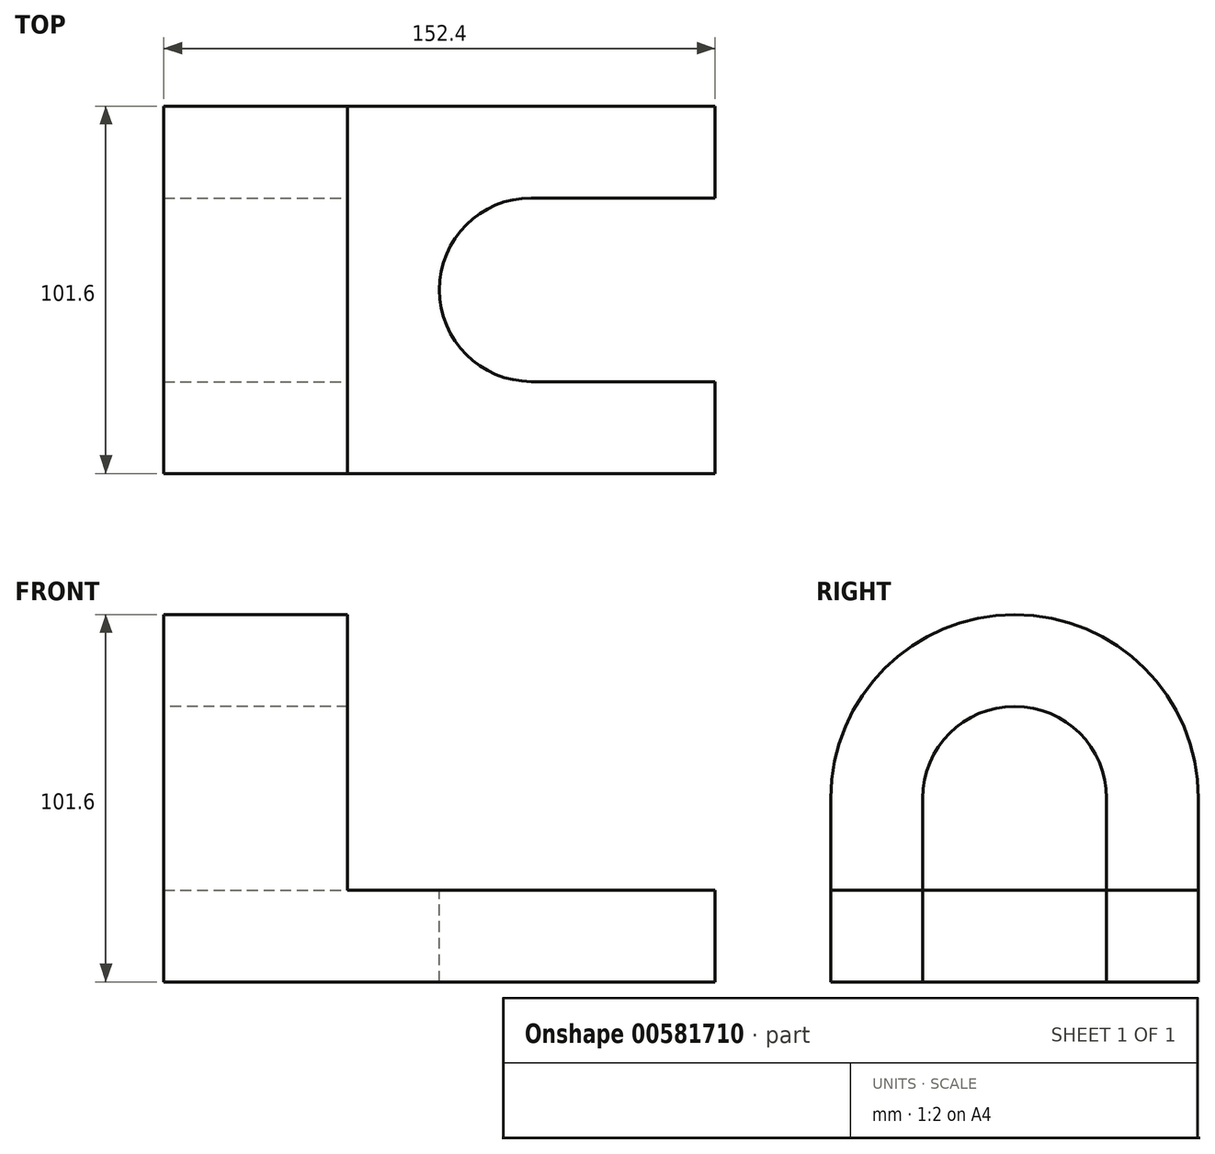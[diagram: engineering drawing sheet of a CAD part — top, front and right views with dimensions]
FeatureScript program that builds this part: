
annotation { "Feature Type Name" : "Feature", "Feature Type Description" : "" }
export const myFeature = defineFeature(function(context is Context, id is Id, definition is map)
    precondition{}
    {
        {
            var Q0;
            Q0=qCreatedBy(makeId("Front.planeOp"),FACE);
            var sketch = newSketch(context, id + "F0", { "sketchPlane" : qUnion([Q0])});
            skLineSegment(sketch, "E0.bottom", {"start": v(-25.4, 50.8) * mm, "end": v(-76.2, 50.8) * mm});
            skLineSegment(sketch, "E0.top", {"start": v(76.2, -50.8) * mm, "end": v(-76.2, -50.8) * mm});
            skLineSegment(sketch, "E0.left", {"start": v(76.2, -25.4) * mm, "end": v(76.2, -50.8) * mm});
            skLineSegment(sketch, "E0.right", {"start": v(-76.2, 50.8) * mm, "end": v(-76.2, -50.8) * mm});
            skPoint(sketch, "E0.middle", {"position": v(0, 0) * mm});
            skLineSegment(sketch, "E1", {"start": v(-25.4, 50.8) * mm, "end": v(-25.4, -25.4) * mm});
            skLineSegment(sketch, "E2", {"start": v(-25.4, -25.4) * mm, "end": v(76.2, -25.4) * mm});
            skPoint(sketch, "E3.orphan", {"position": v(76.2, 50.8) * mm});
            skSolve(sketch);
        }
        {
            var Q0;
            Q0=makeQuery(id+"F0.imprint","IMPRINT",FACE,{"disambiguationData":[TD([[makeQuery(id+"F0.imprint","IMPRINT",EDGE,{"derivedFrom":sQuery(id+"F0.wireOp",EDGE,"E0.bottom")}),1.0]])]});
            extrude(context, id + "F1", {"entities" : qUnion([Q0]), "depth" : 101.6 * mm, "offsetDistance" : 25.4 * mm, "symmetric" : true});
        }
        {
            var Q0;
            Q0=makeQuery(id+"F1.opExtrude","SWEPT_FACE",FACE,{"disambiguationData":[OSD([sQuery(id+"F0.wireOp",EDGE,"E1")])]});
            var sketch = newSketch(context, id + "F2", { "sketchPlane" : qUnion([Q0])});
            skLineSegment(sketch, "E4.bottom", {"start": v(25.4, 25.4) * mm, "end": v(-25.4, 25.4) * mm});
            skLineSegment(sketch, "E4.top", {"start": v(25.4, -25.4) * mm, "end": v(-25.4, -25.4) * mm});
            skLineSegment(sketch, "E4.left", {"start": v(25.4, 25.4) * mm, "end": v(25.4, -25.4) * mm});
            skLineSegment(sketch, "E4.right", {"start": v(-25.4, 25.4) * mm, "end": v(-25.4, -25.4) * mm});
            skPoint(sketch, "E4.middle", {"position": v(0, 0) * mm});
            skSolve(sketch);
        }
        {
            var Q0;
            Q0=makeQuery(id+"F2.imprint","IMPRINT",FACE,{"disambiguationData":[TD([[makeQuery(id+"F2.imprint","IMPRINT",EDGE,{"derivedFrom":sQuery(id+"F2.wireOp",EDGE,"E4.bottom")}),1.0]])]});
            extrude(context, id + "F3", {"entities" : qUnion([Q0]), "operationType" : NewBodyOperationType.REMOVE, "oppositeDirection" : true, "depth" : 204.5 * mm, "offsetDistance" : 25.4 * mm});
        }
        {
            var Q0;
            Q0=makeQuery(id+"F3.boolean.opBoolean","MERGE",FACE,{"derivedFrom":[makeQuery(id+"F1.opExtrude","SWEPT_FACE",FACE,{"disambiguationData":[OSD([sQuery(id+"F0.wireOp",EDGE,"E2")])]}),makeQuery(id+"F3.opExtrude","SWEPT_FACE",FACE,{"disambiguationData":[OSD([sQuery(id+"F2.wireOp",EDGE,"E4.top")])]})]});
            var sketch = newSketch(context, id + "F4", { "sketchPlane" : qUnion([Q0])});
            skLineSegment(sketch, "E5.bottom", {"start": v(76.2, 25.4) * mm, "end": v(0, 25.4) * mm});
            skLineSegment(sketch, "E5.top", {"start": v(76.2, -25.4) * mm, "end": v(0, -25.4) * mm});
            skLineSegment(sketch, "E5.left", {"start": v(76.2, 25.4) * mm, "end": v(76.2, -25.4) * mm});
            skLineSegment(sketch, "E5.right", {"start": v(0, 25.4) * mm, "end": v(0, -25.4) * mm});
            skPoint(sketch, "E5.middle", {"position": v(38.1, 0) * mm});
            skSolve(sketch);
        }
        {
            var Q0;
            Q0=makeQuery(id+"F4.imprint","IMPRINT",FACE,{"disambiguationData":[TD([[makeQuery(id+"F4.imprint","IMPRINT",EDGE,{"derivedFrom":sQuery(id+"F4.wireOp",EDGE,"E5.bottom")}),1.0]])]});
            extrude(context, id + "F5", {"entities" : qUnion([Q0]), "operationType" : NewBodyOperationType.REMOVE, "oppositeDirection" : true, "depth" : 61.38 * mm, "offsetDistance" : 25.4 * mm});
        }
        {
            var Q0;
            Q0=makeQuery(id+"F1.opExtrude","CAP_EDGE",EDGE,{"disambiguationData":[OSD([sQuery(id+"F0.wireOp",EDGE,"E0.bottom")])],"isStart":false});
            var Q1;
            Q1=makeQuery(id+"F1.opExtrude","CAP_EDGE",EDGE,{"disambiguationData":[OSD([sQuery(id+"F0.wireOp",EDGE,"E0.bottom")])],"isStart":true});
            fillet(context, id + "F6", {"entities" : qUnion([Q0, Q1]), "radius" : 50.8 * mm, "tangentPropagation" : true, "allowEdgeOverflow" : false});
        }
        {
            var Q0;
            Q0=makeQuery(id+"F3.boolean.opBoolean","COPY",EDGE,{"derivedFrom":makeQuery(id+"F3.opExtrude","SWEPT_EDGE",EDGE,{"disambiguationData":[OSD([sQuery(id+"F2.wireOp",EDGE,"E4.bottom"),sQuery(id+"F2.wireOp",EDGE,"E4.right")])]})});
            var Q1;
            Q1=makeQuery(id+"F3.boolean.opBoolean","COPY",EDGE,{"derivedFrom":makeQuery(id+"F3.opExtrude","SWEPT_EDGE",EDGE,{"disambiguationData":[OSD([sQuery(id+"F2.wireOp",EDGE,"E4.bottom"),sQuery(id+"F2.wireOp",EDGE,"E4.left")])]})});
            fillet(context, id + "F7", {"entities" : qUnion([Q0, Q1]), "radius" : 25.4 * mm, "tangentPropagation" : true, "allowEdgeOverflow" : false});
        }
        {
            var Q0;
            Q0=makeQuery(id+"F5.boolean.opBoolean","COPY",EDGE,{"derivedFrom":makeQuery(id+"F5.opExtrude","SWEPT_EDGE",EDGE,{"disambiguationData":[OSD([sQuery(id+"F4.wireOp",EDGE,"E5.top"),sQuery(id+"F4.wireOp",EDGE,"E5.right")])]})});
            var Q1;
            Q1=makeQuery(id+"F5.boolean.opBoolean","COPY",EDGE,{"derivedFrom":makeQuery(id+"F5.opExtrude","SWEPT_EDGE",EDGE,{"disambiguationData":[OSD([sQuery(id+"F4.wireOp",EDGE,"E5.bottom"),sQuery(id+"F4.wireOp",EDGE,"E5.right")])]})});
            fillet(context, id + "F8", {"entities" : qUnion([Q0, Q1]), "radius" : 25.4 * mm, "tangentPropagation" : true, "allowEdgeOverflow" : false});
        }
    });
